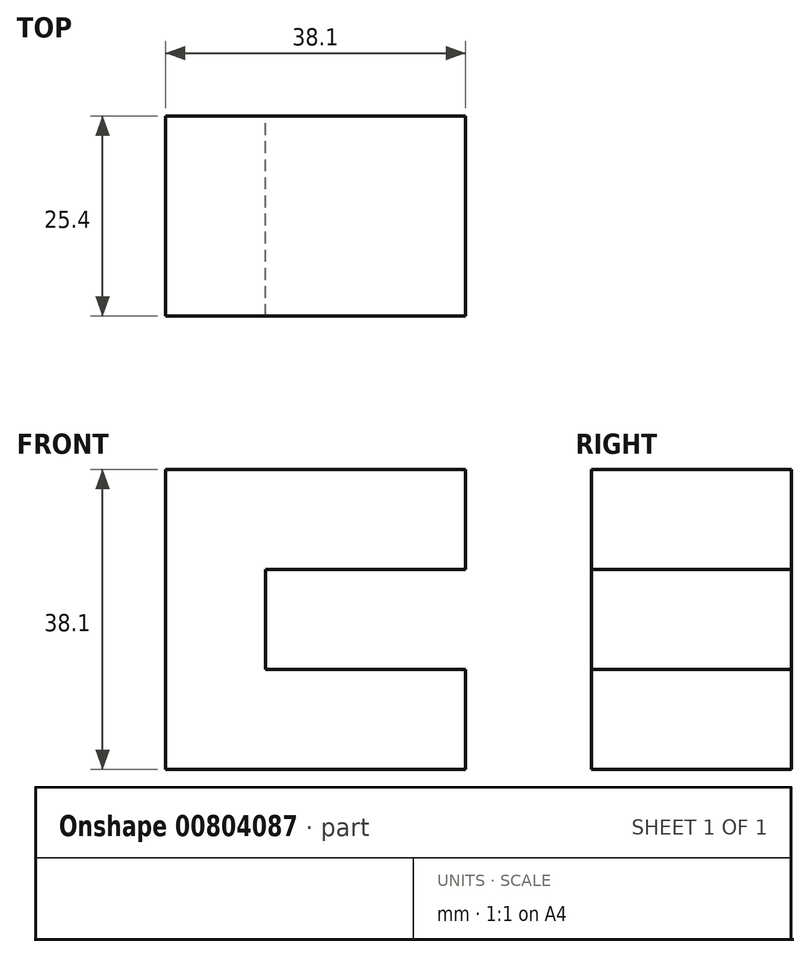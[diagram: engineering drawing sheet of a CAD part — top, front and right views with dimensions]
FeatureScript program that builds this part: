
annotation { "Feature Type Name" : "Feature", "Feature Type Description" : "" }
export const myFeature = defineFeature(function(context is Context, id is Id, definition is map)
    precondition{}
    {
        {
            var Q0;
            Q0=qCreatedBy(makeId("Front.planeOp"),FACE);
            var sketch = newSketch(context, id + "F0", { "sketchPlane" : qUnion([Q0])});
            skLineSegment(sketch, "E0", {"start": v(0, 0) * mm, "end": v(38.1, 0) * mm});
            skLineSegment(sketch, "E1", {"start": v(38.1, 0) * mm, "end": v(38.1, 12.7) * mm});
            skLineSegment(sketch, "E2", {"start": v(38.1, 12.7) * mm, "end": v(12.7, 12.7) * mm});
            skLineSegment(sketch, "E3", {"start": v(12.7, 12.7) * mm, "end": v(12.7, 25.4) * mm});
            skLineSegment(sketch, "E4", {"start": v(12.7, 25.4) * mm, "end": v(38.1, 25.4) * mm});
            skLineSegment(sketch, "E5", {"start": v(38.1, 25.4) * mm, "end": v(38.1, 38.1) * mm});
            skLineSegment(sketch, "E6", {"start": v(38.1, 38.1) * mm, "end": v(0, 38.1) * mm});
            skLineSegment(sketch, "E7", {"start": v(0, 38.1) * mm, "end": v(0, 0) * mm});
            skSolve(sketch);
        }
        {
            var Q0;
            Q0=makeQuery(id+"F0.imprint","IMPRINT",FACE,{"disambiguationData":[TD([[makeQuery(id+"F0.imprint","IMPRINT",EDGE,{"derivedFrom":sQuery(id+"F0.wireOp",EDGE,"E0")}),1.0]])]});
            extrude(context, id + "F1", {"entities" : qUnion([Q0]), "depth" : 25.4 * mm, "offsetDistance" : 25.4 * mm});
        }
    });
